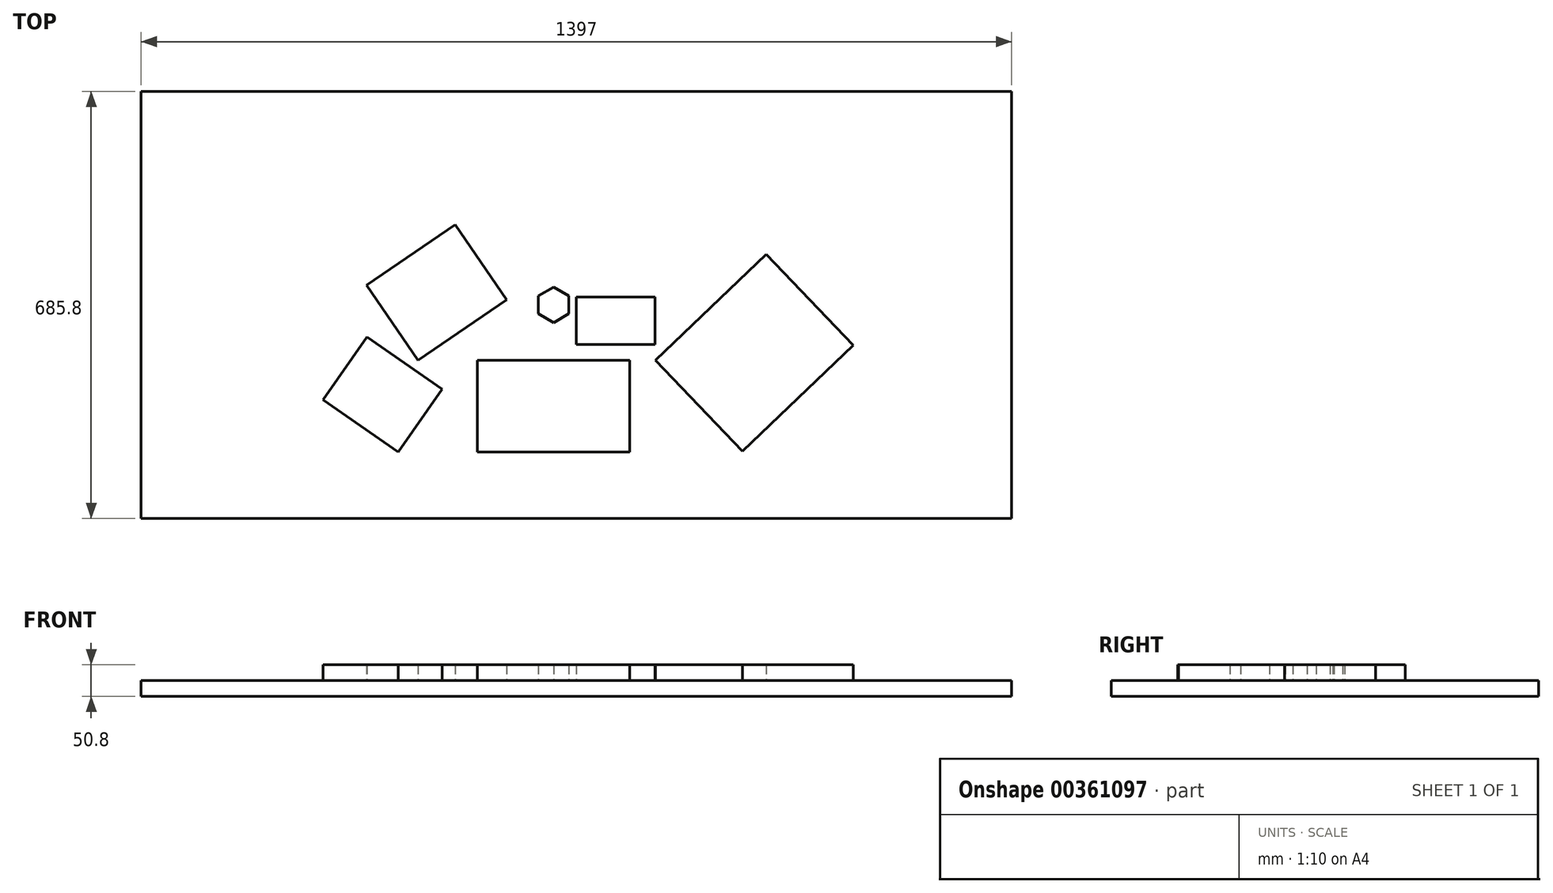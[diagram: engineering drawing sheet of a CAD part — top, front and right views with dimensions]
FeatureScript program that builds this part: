
annotation { "Feature Type Name" : "Feature", "Feature Type Description" : "" }
export const myFeature = defineFeature(function(context is Context, id is Id, definition is map)
    precondition{}
    {
        {
            var Q0;
            Q0=qCreatedBy(makeId("Top.planeOp"),FACE);
            var sketch = newSketch(context, id + "F0", { "sketchPlane" : qUnion([Q0])});
            skLineSegment(sketch, "E0.bottom", {"start": v(735.06, 342.9) * mm, "end": v(-661.94, 342.9) * mm});
            skLineSegment(sketch, "E0.top", {"start": v(735.06, -342.9) * mm, "end": v(-661.94, -342.9) * mm});
            skLineSegment(sketch, "E0.left", {"start": v(735.06, 342.9) * mm, "end": v(735.06, -342.9) * mm});
            skLineSegment(sketch, "E0.right", {"start": v(-661.94, 342.9) * mm, "end": v(-661.94, -342.9) * mm});
            skPoint(sketch, "E0.middle", {"position": v(36.56, 0) * mm});
            skSolve(sketch);
        }
        {
            var Q0;
            Q0 = qSketchRegion(id + "F0", true);
            extrude(context, id + "F1", {"entities" : qUnion([Q0]), "depth" : 25.4 * mm});
        }
        {
            var Q0;
            Q0=makeQuery(id+"F1.opExtrude","CAP_FACE",FACE,{"disambiguationData":[OSD([sQuery(id+"F0.wireOp",EDGE,"E0.bottom"),sQuery(id+"F0.wireOp",EDGE,"E0.top"),sQuery(id+"F0.wireOp",EDGE,"E0.left"),sQuery(id+"F0.wireOp",EDGE,"E0.right")])],"isStart":false});
            var sketch = newSketch(context, id + "F2", { "sketchPlane" : qUnion([Q0])});
            skLineSegment(sketch, "E1.bottom", {"start": v(122.19, -88.9) * mm, "end": v(-122.19, -88.9) * mm});
            skLineSegment(sketch, "E1.top", {"start": v(122.19, -236.25) * mm, "end": v(-122.19, -236.25) * mm});
            skLineSegment(sketch, "E1.left", {"start": v(122.19, -88.9) * mm, "end": v(122.19, -236.25) * mm});
            skLineSegment(sketch, "E1.right", {"start": v(-122.19, -88.9) * mm, "end": v(-122.19, -236.25) * mm});
            skPoint(sketch, "E1.middle", {"position": v(0, -162.58) * mm});
            skLineSegment(sketch, "E2.bottom", {"start": v(303.26, -234.95) * mm, "end": v(163.56, -88.9) * mm});
            skLineSegment(sketch, "E2.top", {"start": v(481.12, -64.82) * mm, "end": v(341.42, 81.23) * mm});
            skLineSegment(sketch, "E2.left", {"start": v(303.26, -234.95) * mm, "end": v(481.12, -64.82) * mm});
            skLineSegment(sketch, "E2.right", {"start": v(163.56, -88.9) * mm, "end": v(341.42, 81.23) * mm});
            skPoint(sketch, "E2.middle", {"position": v(322.34, -76.86) * mm});
            skLineSegment(sketch, "E3.bottom", {"start": v(-75.25, 8.39) * mm, "end": v(-217.44, -88.9) * mm});
            skLineSegment(sketch, "E3.top", {"start": v(-157.8, 129.04) * mm, "end": v(-299.99, 31.75) * mm});
            skLineSegment(sketch, "E3.left", {"start": v(-75.25, 8.39) * mm, "end": v(-157.8, 129.04) * mm});
            skLineSegment(sketch, "E3.right", {"start": v(-217.44, -88.9) * mm, "end": v(-299.99, 31.75) * mm});
            skPoint(sketch, "E3.middle", {"position": v(-187.62, 20.07) * mm});
            skLineSegment(sketch, "E4.bottom", {"start": v(-178.96, -135.2) * mm, "end": v(-249.19, -236.25) * mm});
            skLineSegment(sketch, "E4.top", {"start": v(-299.6, -51.35) * mm, "end": v(-369.84, -152.4) * mm});
            skLineSegment(sketch, "E4.left", {"start": v(-178.96, -135.2) * mm, "end": v(-299.6, -51.35) * mm});
            skLineSegment(sketch, "E4.right", {"start": v(-249.19, -236.25) * mm, "end": v(-369.84, -152.4) * mm});
            skPoint(sketch, "E4.middle", {"position": v(-274.4, -143.8) * mm});
            skCircle(sketch, "E5.cCircle", {"center": v(0, 0) * mm, "radius": 24.61 * mm, "construction": true});
            skLineSegment(sketch, "E5.0", {"start": v(24.61, 14.2) * mm, "end": v(24.61, -14.2) * mm});
            skLineSegment(sketch, "E5.1", {"start": v(24.61, -14.2) * mm, "end": v(0, -28.42) * mm});
            skLineSegment(sketch, "E5.2", {"start": v(0, -28.42) * mm, "end": v(-24.61, -14.2) * mm});
            skLineSegment(sketch, "E5.3", {"start": v(-24.61, -14.2) * mm, "end": v(-24.61, 14.2) * mm});
            skLineSegment(sketch, "E5.4", {"start": v(-24.61, 14.2) * mm, "end": v(0, 28.42) * mm});
            skLineSegment(sketch, "E5.5", {"start": v(0, 28.42) * mm, "end": v(24.61, 14.2) * mm});
            skPoint(sketch, "E5.0.midPoint", {"position": v(24.61, 0) * mm});
            skLineSegment(sketch, "E6.bottom", {"start": v(162.44, -63.5) * mm, "end": v(36.56, -63.5) * mm});
            skLineSegment(sketch, "E6.top", {"start": v(162.44, 12.7) * mm, "end": v(36.56, 12.7) * mm});
            skLineSegment(sketch, "E6.left", {"start": v(162.44, -63.5) * mm, "end": v(162.44, 12.7) * mm});
            skLineSegment(sketch, "E6.right", {"start": v(36.56, -63.5) * mm, "end": v(36.56, 12.7) * mm});
            skPoint(sketch, "E6.middle", {"position": v(99.5, -25.4) * mm});
            skSolve(sketch);
        }
        {
            var Q0;
            Q0 = qSketchRegion(id + "F2", true);
            extrude(context, id + "F3", {"entities" : qUnion([Q0]), "depth" : 25.4 * mm});
        }
    });
